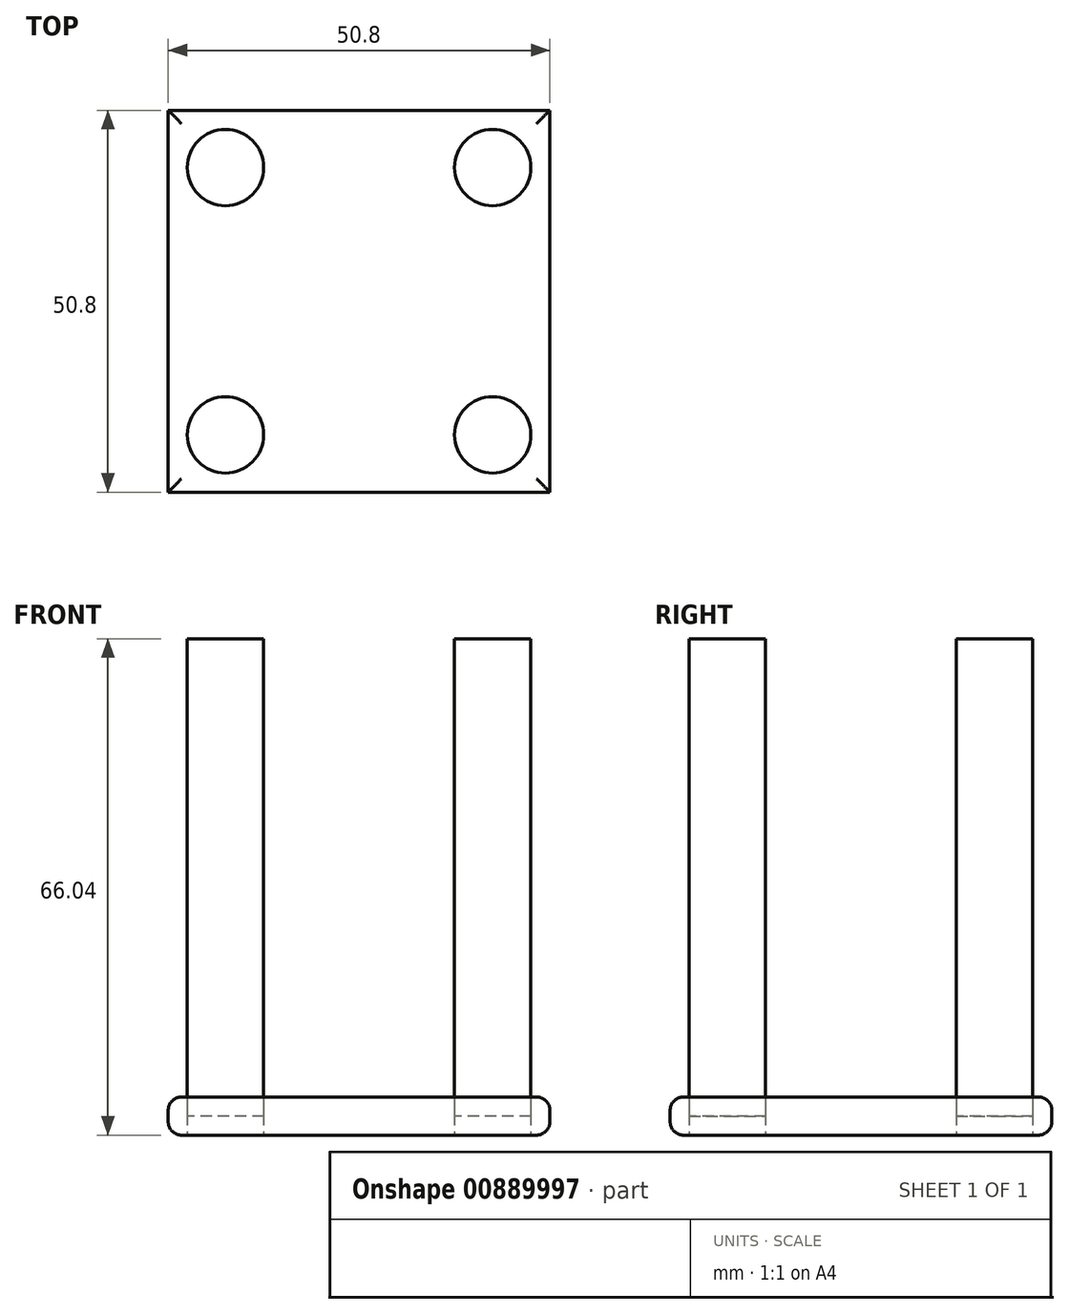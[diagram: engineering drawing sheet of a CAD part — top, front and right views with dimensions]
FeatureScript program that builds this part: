
annotation { "Feature Type Name" : "Feature", "Feature Type Description" : "" }
export const myFeature = defineFeature(function(context is Context, id is Id, definition is map)
    precondition{}
    {
        {
            var Q0;
            Q0=qCreatedBy(makeId("Top.planeOp"),FACE);
            var sketch = newSketch(context, id + "F0", { "sketchPlane" : qUnion([Q0])});
            skLineSegment(sketch, "E0.bottom", {"start": v(-25.4, 25.4) * mm, "end": v(25.4, 25.4) * mm});
            skLineSegment(sketch, "E0.top", {"start": v(-25.4, -25.4) * mm, "end": v(25.4, -25.4) * mm});
            skLineSegment(sketch, "E0.left", {"start": v(-25.4, 25.4) * mm, "end": v(-25.4, -25.4) * mm});
            skLineSegment(sketch, "E0.right", {"start": v(25.4, 25.4) * mm, "end": v(25.4, -25.4) * mm});
            skPoint(sketch, "E0.middle", {"position": v(0, 0) * mm});
            skCircle(sketch, "E1", {"center": v(-17.78, 17.78) * mm, "radius": 5.08 * mm});
            skCircle(sketch, "E2", {"center": v(17.78, 17.78) * mm, "radius": 5.08 * mm});
            skCircle(sketch, "E3", {"center": v(-17.78, -17.78) * mm, "radius": 5.08 * mm});
            skCircle(sketch, "E4", {"center": v(17.78, -17.78) * mm, "radius": 5.08 * mm});
            skSolve(sketch);
        }
        {
            var Q0;
            Q0=makeQuery(id+"F0.imprint","IMPRINT",FACE,{"disambiguationData":[TD([[makeQuery(id+"F0.imprint","IMPRINT",EDGE,{"derivedFrom":sQuery(id+"F0.wireOp",EDGE,"E1")}),1.0]])]});
            var Q1;
            Q1=makeQuery(id+"F0.imprint","IMPRINT",FACE,{"disambiguationData":[TD([[makeQuery(id+"F0.imprint","IMPRINT",EDGE,{"derivedFrom":sQuery(id+"F0.wireOp",EDGE,"E2")}),1.0]])]});
            var Q2;
            Q2=makeQuery(id+"F0.imprint","IMPRINT",FACE,{"disambiguationData":[TD([[makeQuery(id+"F0.imprint","IMPRINT",EDGE,{"derivedFrom":sQuery(id+"F0.wireOp",EDGE,"E4")}),1.0]])]});
            var Q3;
            Q3=makeQuery(id+"F0.imprint","IMPRINT",FACE,{"disambiguationData":[TD([[makeQuery(id+"F0.imprint","IMPRINT",EDGE,{"derivedFrom":sQuery(id+"F0.wireOp",EDGE,"E3")}),1.0]])]});
            extrude(context, id + "F1", {"entities" : qUnion([Q0, Q1, Q2, Q3]), "depth" : 63.5 * mm, "offsetDistance" : 25.4 * mm});
        }
        {
            var Q0;
            Q0 = qSketchRegion(id + "F0", true);
            extrude(context, id + "F2", {"entities" : qUnion([Q0]), "endBound" : BoundingType.SYMMETRIC, "depth" : 5.08 * mm, "offsetDistance" : 25.4 * mm});
        }
        {
            var Q0;
            Q0=makeQuery(id+"F2.opExtrude","CAP_EDGE",EDGE,{"disambiguationData":[OSD([sQuery(id+"F0.wireOp",EDGE,"E0.left")])],"isStart":true});
            var Q1;
            Q1=makeQuery(id+"F2.opExtrude","CAP_EDGE",EDGE,{"disambiguationData":[OSD([sQuery(id+"F0.wireOp",EDGE,"E0.top")])],"isStart":true});
            var Q2;
            Q2=makeQuery(id+"F2.opExtrude","CAP_EDGE",EDGE,{"disambiguationData":[OSD([sQuery(id+"F0.wireOp",EDGE,"E0.right")])],"isStart":true});
            var Q3;
            Q3=makeQuery(id+"F2.opExtrude","CAP_EDGE",EDGE,{"disambiguationData":[OSD([sQuery(id+"F0.wireOp",EDGE,"E0.bottom")])],"isStart":true});
            var Q4;
            Q4=makeQuery(id+"F2.opExtrude","CAP_EDGE",EDGE,{"disambiguationData":[OSD([sQuery(id+"F0.wireOp",EDGE,"E0.top")])],"isStart":false});
            var Q5;
            Q5=makeQuery(id+"F2.opExtrude","CAP_EDGE",EDGE,{"disambiguationData":[OSD([sQuery(id+"F0.wireOp",EDGE,"E0.right")])],"isStart":false});
            var Q6;
            Q6=makeQuery(id+"F2.opExtrude","CAP_EDGE",EDGE,{"disambiguationData":[OSD([sQuery(id+"F0.wireOp",EDGE,"E0.bottom")])],"isStart":false});
            var Q7;
            Q7=makeQuery(id+"F2.opExtrude","CAP_EDGE",EDGE,{"disambiguationData":[OSD([sQuery(id+"F0.wireOp",EDGE,"E0.left")])],"isStart":false});
            fillet(context, id + "F3", {"entities" : qUnion([Q0, Q1, Q2, Q3, Q4, Q5, Q6, Q7]), "radius" : 1.78 * mm, "tangentPropagation" : true, "allowEdgeOverflow" : false});
        }
    });
